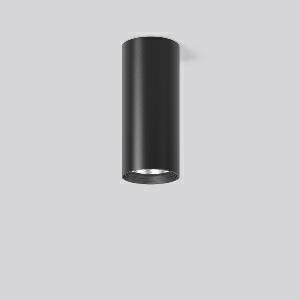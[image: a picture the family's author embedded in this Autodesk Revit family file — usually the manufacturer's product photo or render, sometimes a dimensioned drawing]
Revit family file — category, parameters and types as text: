
# Revit family: heledon_mini_a_931208_003_2_de48
name_source: partatom
category: Lighting Fixtures
units: mm (PartAtom-declared; Revit-internal decimal feet)

## family parameters
Cut with Voids When Loaded = No
Host = Face
Light Source = No
Part Type = Normal
Room Calculation Point = No
Round Connector Dimension = Use Diameter
Shared = No

## types (1)
- HELEDON mini A (1 x LED Modul 927, 3400 lm, 2700)
    Apparent Load = 29 VA
    Approval mark = CE
    CIE Flux Codes = 100 100 100 100 100
    Color Rendering = 92
    Color Temperature = 2700
    Default Elevation = 1800 mm
    Description = Series: HELEDON mini
Cylindrical surface-mounted downlight. Housing: die-cast aluminium, powder-coated. Internal ceiling frame polycarbonate with bayonet mounting. Black plastic ring and recessed LED to prevent glare from the side. Optical assembly with reflector made of MIRO-Silver with 98% total light reflection for outstanding efficiency - can be changed without tools. Best colour rendering index Ra>90. Suitable for Ceiling mounting. Easy installation with a separate ceiling frame with bayonet mounting and plug connection. Driver integrated. Connected via plug-in connector. High quality converter without flickering and stroboscopic effect. The following accessories can be mounted without use of tools: interchangeable lenses, decorative glasses, honeycomb louvre, clear and frosted diffusers, white interchangeable plastic ring. 
Colour: deep black, matt (RAL 9005)
Diameter: 87 mm
Height: 197 mm
Lamp: LED
Socket: without socket
Colour temperature: 2700K
Colour rendering index (CRI): 92
System power: 29 W
Rated luminous flux: 3400 lm
Luminous efficiency: 117 lm/W
Control gear: Regulated power supply
Protection class: I
Type of protection: IP 20
    Height = 197 mm
    Lamp = 1 x LED Modul 927
    Lamp Light Flux = 3400 lm
    Lamp count = 1
    Length = 87 mm
    Lifetime = 50000 h
    Luminous efficacy = 117 lm/W
    Manufacturer = RZB
    ModVariant = No
    Model = 931208.003.2
    Mounting Place = Ceiling
    Mounting Type = Surface mounted
    Number of Poles = 1
    OnlyDefault = Yes
    Power Factor = 1
    Product Name = HELEDON mini A
    Product group = Surface mounted downlights
    ProductGroupID = 302
    Protection Class = Protection class I
    Protection Degree = IP 20
    RLX_Detail_Level = 1
    RLX_Emergency_Light_Flux = 0 lm
    RLX_Emergency_Type = 0
    RLX_Emergency_Type_DB = No
    RlxData = <blob elided: 106109 chars, md5=55899e72>
    Socket = socket
    Standby Power = 0 W
    System Light Flux = 3400 lm
    System Power = 29 W
    Type Comments = Product without accessories
    Type Image = 931188.003.jpg
    URL = http://relux.com
    VarID = ---
    Voltage = 230 V
    Voltage Range = 220-240 V
    Weight = 0.00 kg
    Width = 0 mm  [stored 0 ft]

note: [stored X ft] marks values corroborated as IEEE doubles in the binary element streams (Revit-internal decimal feet)

## geometry (parser evidence)
native form markers: Blend x4, Sweep x9
no freeform markers — native parametric forms only
